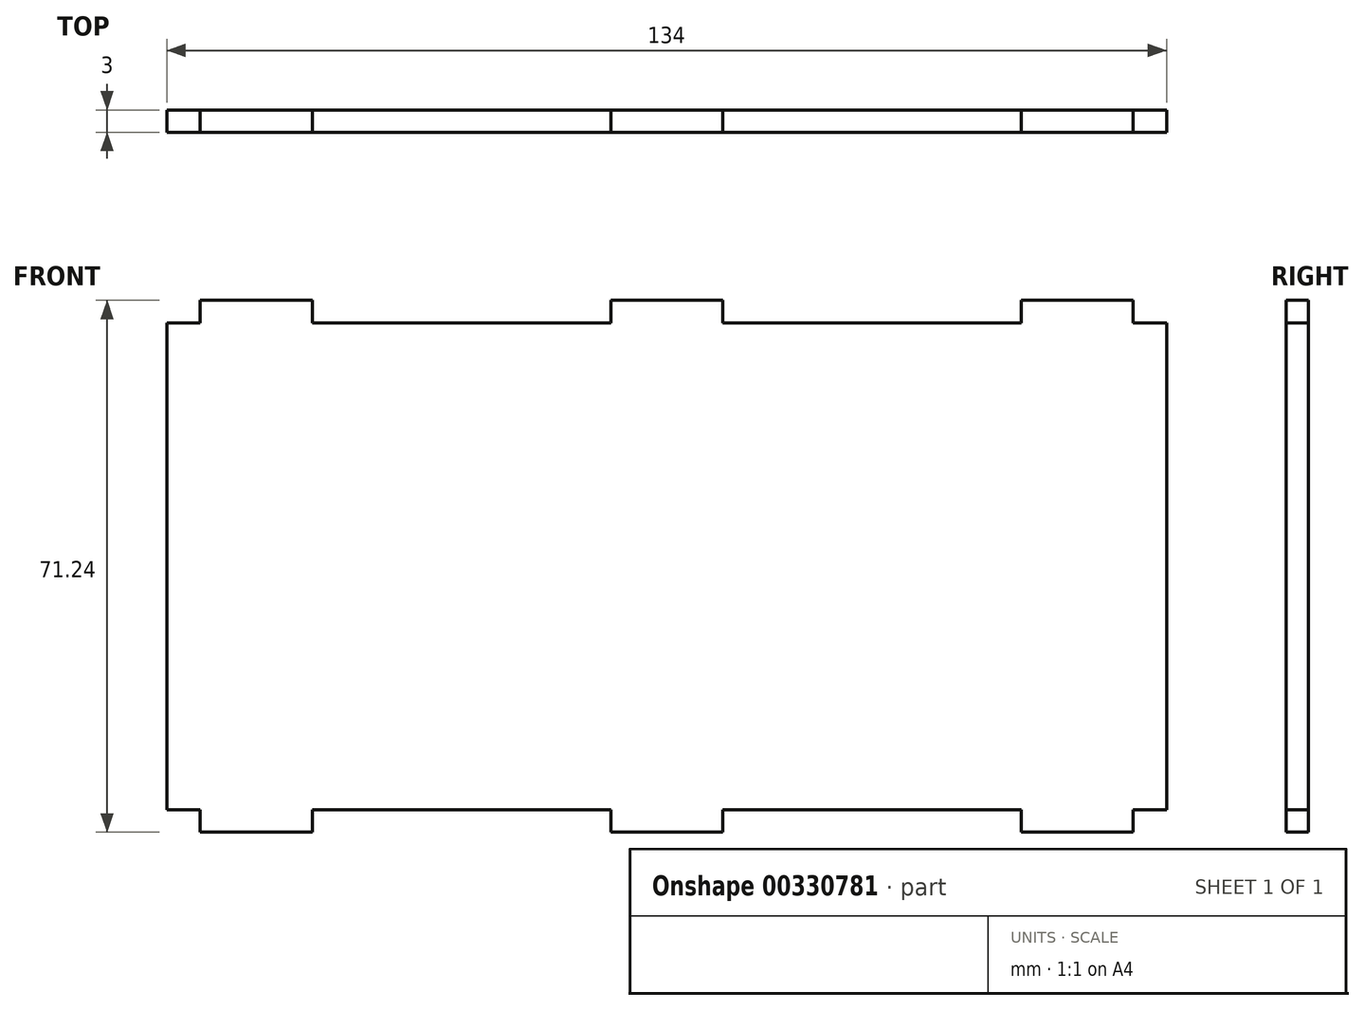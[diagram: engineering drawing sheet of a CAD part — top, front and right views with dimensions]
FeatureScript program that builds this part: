
annotation { "Feature Type Name" : "Feature", "Feature Type Description" : "" }
export const myFeature = defineFeature(function(context is Context, id is Id, definition is map)
    precondition{}
    {
        {
            var Q0;
            Q0=qCreatedBy(makeId("Front.planeOp"),FACE);
            var sketch = newSketch(context, id + "F0", { "sketchPlane" : qUnion([Q0])});
            skLineSegment(sketch, "E0.bottom", {"start": v(-67, 32.62) * mm, "end": v(67, 32.62) * mm});
            skLineSegment(sketch, "E0.top", {"start": v(-67, -32.62) * mm, "end": v(67, -32.62) * mm});
            skLineSegment(sketch, "E0.left", {"start": v(-67, 32.62) * mm, "end": v(-67, -32.62) * mm});
            skLineSegment(sketch, "E0.right", {"start": v(67, 32.62) * mm, "end": v(67, -32.62) * mm});
            skPoint(sketch, "E0.middle", {"position": v(0, 0) * mm});
            skLineSegment(sketch, "E1.bottom", {"start": v(-62.5, -32.62) * mm, "end": v(-47.5, -32.62) * mm});
            skLineSegment(sketch, "E1.top", {"start": v(-62.5, -35.63) * mm, "end": v(-47.5, -35.63) * mm});
            skLineSegment(sketch, "E1.left", {"start": v(-62.5, -32.62) * mm, "end": v(-62.5, -35.63) * mm});
            skLineSegment(sketch, "E1.right", {"start": v(-47.5, -32.62) * mm, "end": v(-47.5, -35.62) * mm});
            skLineSegment(sketch, "E2.0.1.0", {"start": v(-62.5, 35.63) * mm, "end": v(-62.5, 32.62) * mm});
            skLineSegment(sketch, "E2.0.1.1", {"start": v(-62.5, 35.63) * mm, "end": v(-47.5, 35.63) * mm});
            skLineSegment(sketch, "E2.0.1.2", {"start": v(-47.5, 35.63) * mm, "end": v(-47.5, 32.63) * mm});
            skLineSegment(sketch, "E2.0.1.3", {"start": v(-62.5, 32.63) * mm, "end": v(-47.5, 32.63) * mm});
            skLineSegment(sketch, "E2.1.0.0", {"start": v(-7.5, -32.62) * mm, "end": v(-7.5, -35.63) * mm});
            skLineSegment(sketch, "E2.1.0.1", {"start": v(-7.5, -32.62) * mm, "end": v(7.5, -32.62) * mm});
            skLineSegment(sketch, "E2.1.0.2", {"start": v(7.5, -32.62) * mm, "end": v(7.5, -35.63) * mm});
            skLineSegment(sketch, "E2.1.0.3", {"start": v(-7.5, -35.63) * mm, "end": v(7.5, -35.63) * mm});
            skLineSegment(sketch, "E2.1.1.0", {"start": v(-7.5, 35.63) * mm, "end": v(-7.5, 32.62) * mm});
            skLineSegment(sketch, "E2.1.1.1", {"start": v(-7.5, 35.63) * mm, "end": v(7.5, 35.63) * mm});
            skLineSegment(sketch, "E2.1.1.2", {"start": v(7.5, 35.63) * mm, "end": v(7.5, 32.63) * mm});
            skLineSegment(sketch, "E2.1.1.3", {"start": v(-7.5, 32.63) * mm, "end": v(7.5, 32.63) * mm});
            skLineSegment(sketch, "E2.2.0.0", {"start": v(47.5, -32.63) * mm, "end": v(47.5, -35.63) * mm});
            skLineSegment(sketch, "E2.2.0.1", {"start": v(47.5, -32.62) * mm, "end": v(62.5, -32.62) * mm});
            skLineSegment(sketch, "E2.2.0.2", {"start": v(62.5, -32.62) * mm, "end": v(62.5, -35.63) * mm});
            skLineSegment(sketch, "E2.2.0.3", {"start": v(47.5, -35.63) * mm, "end": v(62.5, -35.63) * mm});
            skLineSegment(sketch, "E2.2.1.0", {"start": v(47.5, 35.63) * mm, "end": v(47.5, 32.62) * mm});
            skLineSegment(sketch, "E2.2.1.1", {"start": v(47.5, 35.63) * mm, "end": v(62.5, 35.63) * mm});
            skLineSegment(sketch, "E2.2.1.2", {"start": v(62.5, 35.63) * mm, "end": v(62.5, 32.63) * mm});
            skLineSegment(sketch, "E2.2.1.3", {"start": v(47.5, 32.63) * mm, "end": v(62.5, 32.63) * mm});
            skLineSegment(sketch, "E2.direction1", {"start": v(-62.5, -35.63) * mm, "end": v(-7.5, -35.63) * mm, "construction": true});
            skLineSegment(sketch, "E2.direction2", {"start": v(-62.5, -35.63) * mm, "end": v(-62.5, 32.62) * mm, "construction": true});
            skSolve(sketch);
        }
        {
            var Q0;
            Q0 = qSketchRegion(id + "F0", true);
            extrude(context, id + "F1", {"entities" : qUnion([Q0]), "depth" : 3 * mm});
        }
    });
